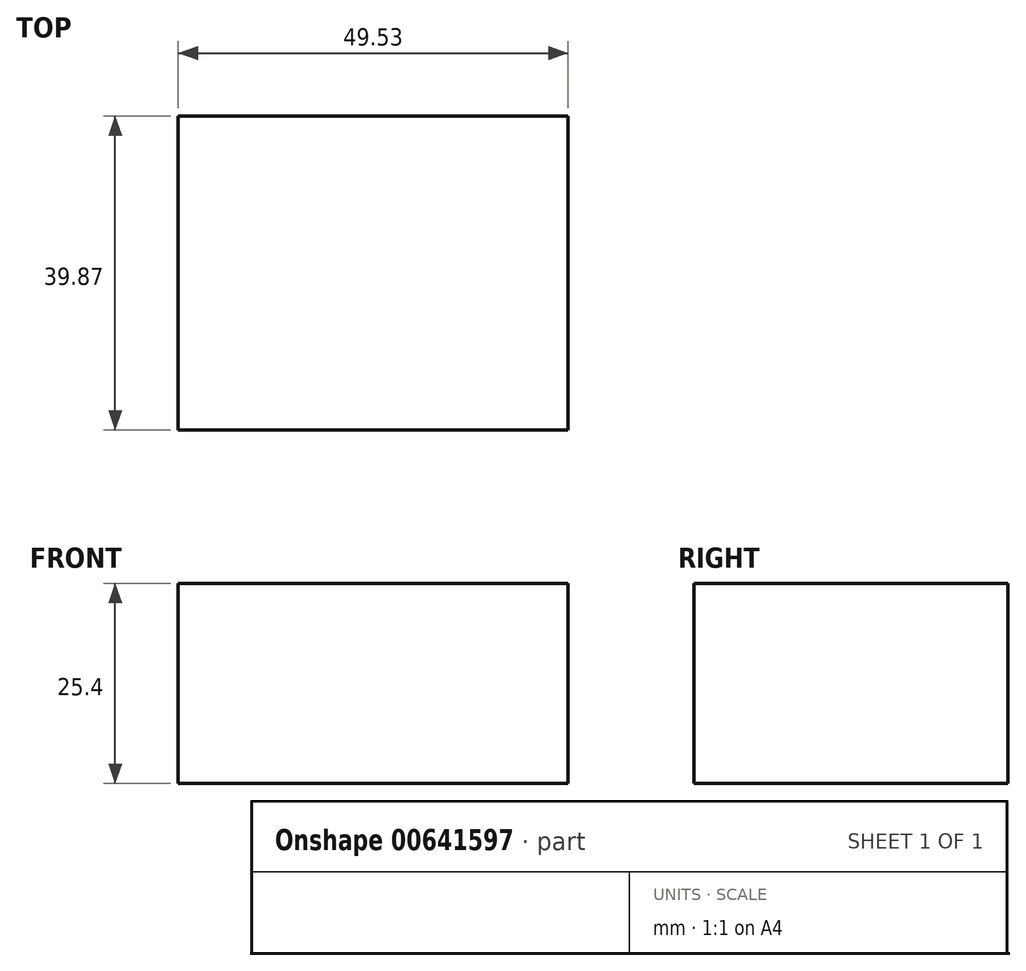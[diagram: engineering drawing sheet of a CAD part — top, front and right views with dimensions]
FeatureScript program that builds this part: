
annotation { "Feature Type Name" : "Feature", "Feature Type Description" : "" }
export const myFeature = defineFeature(function(context is Context, id is Id, definition is map)
    precondition{}
    {
        {
            var Q0;
            Q0=qCreatedBy(makeId("Top.planeOp"),FACE);
            var sketch = newSketch(context, id + "F0", { "sketchPlane" : qUnion([Q0])});
            skLineSegment(sketch, "E0.bottom", {"start": v(0, 0) * mm, "end": v(49.53, 0) * mm});
            skLineSegment(sketch, "E0.top", {"start": v(0, -39.87) * mm, "end": v(49.53, -39.87) * mm});
            skLineSegment(sketch, "E0.left", {"start": v(0, 0) * mm, "end": v(0, -39.87) * mm});
            skLineSegment(sketch, "E0.right", {"start": v(49.53, 0) * mm, "end": v(49.53, -39.87) * mm});
            skSolve(sketch);
        }
        {
            var Q0;
            Q0 = qSketchRegion(id + "F0", true);
            extrude(context, id + "F1", {"entities" : qUnion([Q0]), "depth" : 25.4 * mm, "offsetDistance" : 25.4 * mm});
        }
    });
